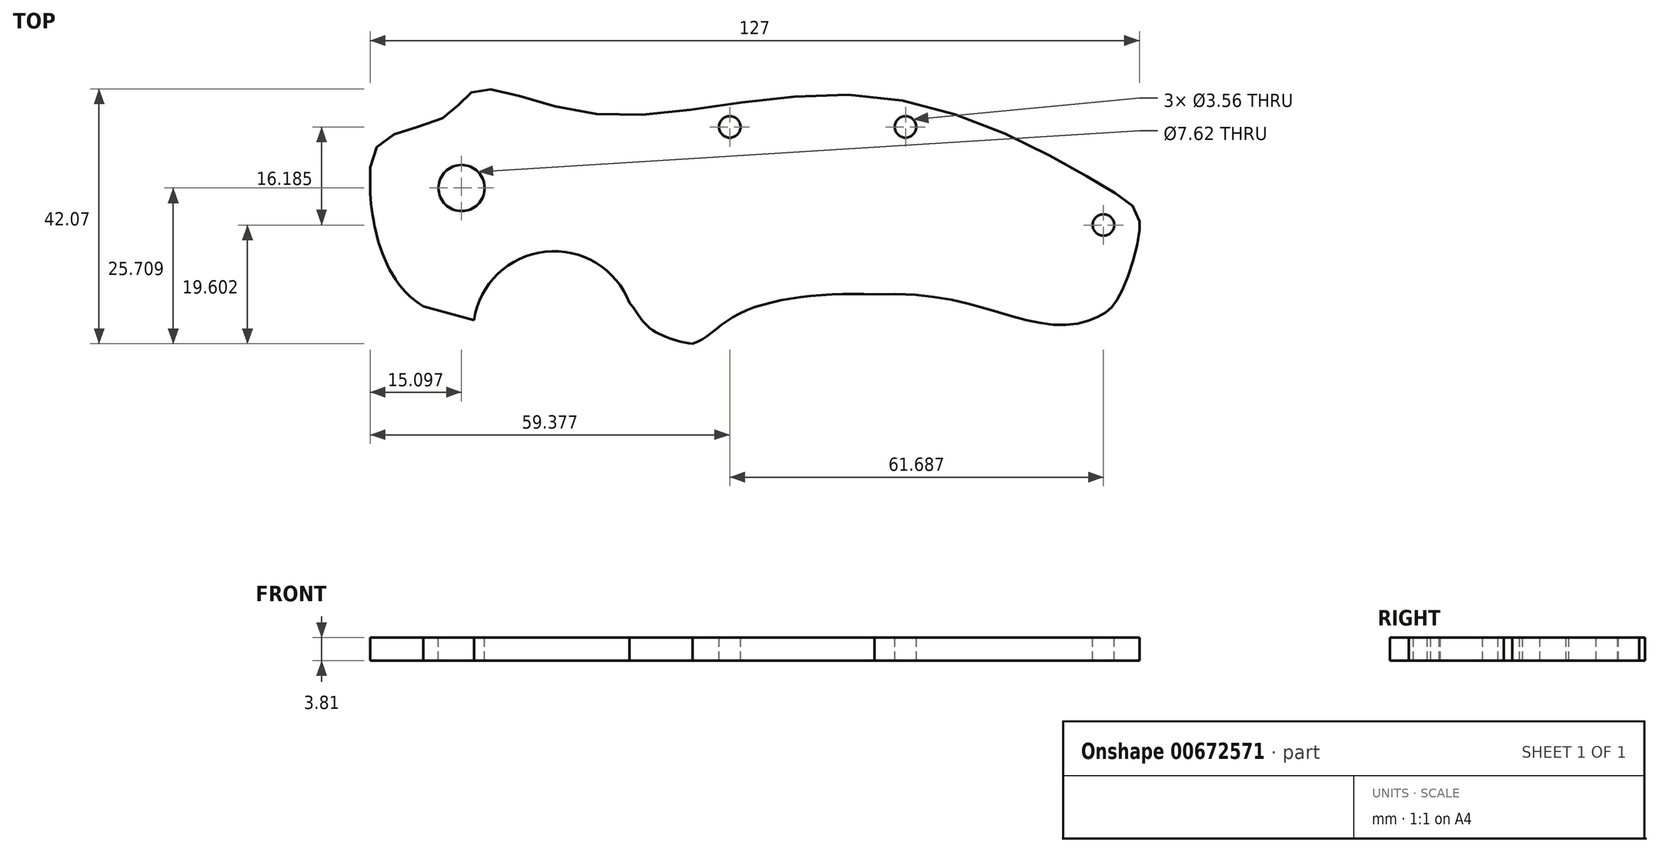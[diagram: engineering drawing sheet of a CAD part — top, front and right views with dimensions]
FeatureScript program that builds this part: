
annotation { "Feature Type Name" : "Feature", "Feature Type Description" : "" }
export const myFeature = defineFeature(function(context is Context, id is Id, definition is map)
    precondition{}
    {
        {
            var Q0;
            Q0=qCreatedBy(makeId("Top.planeOp"),FACE);
            var sketch = newSketch(context, id + "F0", { "sketchPlane" : qUnion([Q0])});
            skLineSegment(sketch, "E0.bottom", {"start": v(63.5, -38.1) * mm, "end": v(-63.5, -38.1) * mm});
            skLineSegment(sketch, "E0.top", {"start": v(63.5, 38.1) * mm, "end": v(-63.5, 38.1) * mm});
            skLineSegment(sketch, "E0.left", {"start": v(63.5, -38.1) * mm, "end": v(63.5, 38.1) * mm});
            skLineSegment(sketch, "E0.right", {"start": v(-63.5, -38.1) * mm, "end": v(-63.5, 38.1) * mm});
            skPoint(sketch, "E0.middle", {"position": v(0, 0) * mm});
            skSolve(sketch);
        }
        {
            var Q0;
            Q0=makeQuery(id+"F0.imprint","IMPRINT",FACE,{"disambiguationData":[TD([[makeQuery(id+"F0.imprint","IMPRINT",EDGE,{"derivedFrom":sQuery(id+"F0.wireOp",EDGE,"E0.bottom")}),-1.0]])]});
            extrude(context, id + "F1", {"entities" : qUnion([Q0]), "depth" : 3.8 * mm, "offsetDistance" : 25.4 * mm});
        }
        {
            var Q0;
            Q0=makeQuery(id+"F1.opExtrude","CAP_FACE",FACE,{"disambiguationData":[OSD([sQuery(id+"F0.wireOp",EDGE,"E0.bottom"),sQuery(id+"F0.wireOp",EDGE,"E0.top"),sQuery(id+"F0.wireOp",EDGE,"E0.left"),sQuery(id+"F0.wireOp",EDGE,"E0.right")])],"isStart":false});
            var sketch = newSketch(context, id + "F2", { "sketchPlane" : qUnion([Q0])});
            skFitSpline(sketch, "E1", {"points": [v(-63.5, 16.64) * mm, v(-61.23, 25.5) * mm, v(-50.85, 29.47) * mm, v(-45.96, 33.74) * mm, v(-26.11, 29.77) * mm, v(21.22, 32.52) * mm, v(59.1, 16.95) * mm, v(63.5, 12.06) * mm, v(60.31, 0) * mm, v(57.56, -3.2) * mm, v(51.46, -5.04) * mm, v(41.07, -3.2) * mm, v(25.5, 0) * mm, v(2.6, -3.51) * mm, v(-6.57, -8.1) * mm, v(-17.56, -5.34) * mm, v(-22.45, 0) * mm, v(-39.24, 0) * mm, v(-44.74, -4.12) * mm, v(-57.26, 0) * mm, v(-63.5, 16.64) * mm]});
            skSolve(sketch);
        }
        {
            var Q0;
            {var subQ5=makeQuery(id+"F1.opExtrude","CAP_EDGE",EDGE,{"disambiguationData":[OSD([sQuery(id+"F0.wireOp",EDGE,"E0.bottom")])],"isStart":false});Q0=makeQuery(id+"F2.imprint","IMPRINT",FACE,{"disambiguationData":[TD([[makeQuery(id+"F2.imprint","IMPRINT",EDGE,{"derivedFrom":subQ5}),-1.0]])]});}
            var Q1;
            {var subQ5=makeQuery(id+"F1.opExtrude","CAP_EDGE",EDGE,{"disambiguationData":[OSD([sQuery(id+"F0.wireOp",EDGE,"E0.top")])],"isStart":false});Q1=makeQuery(id+"F2.imprint","IMPRINT",FACE,{"disambiguationData":[TD([[makeQuery(id+"F2.imprint","IMPRINT",EDGE,{"derivedFrom":subQ5}),1.0]])]});}
            extrude(context, id + "F3", {"entities" : qUnion([Q0, Q1]), "operationType" : NewBodyOperationType.REMOVE, "endBound" : BoundingType.THROUGH_ALL, "oppositeDirection" : true, "depth" : 25.4 * mm, "offsetDistance" : 25.4 * mm});
        }
        {
            var Q0;
            Q0=makeQuery(id+"F1.opExtrude","CAP_FACE",FACE,{"disambiguationData":[OSD([sQuery(id+"F0.wireOp",EDGE,"E0.bottom"),sQuery(id+"F0.wireOp",EDGE,"E0.top"),sQuery(id+"F0.wireOp",EDGE,"E0.left"),sQuery(id+"F0.wireOp",EDGE,"E0.right")])],"isStart":false});
            var sketch = newSketch(context, id + "F4", { "sketchPlane" : qUnion([Q0])});
            skLineSegment(sketch, "E2", {"start": v(-54.7, -1.99) * mm, "end": v(-45.89, -4.38) * mm});
            skCircle(sketch, "E3", {"center": v(-33.13, -6.26) * mm, "radius": 13.38 * mm});
            skEllipse(sketch, "E4", {"center": v(16.34, -12.37) * mm, "majorRadius": 26.48 * mm, "minorRadius": 12.58 * mm, "majorAxis": v(1, 0.13)});
            skSolve(sketch);
        }
        {
            var Q0;
            {var subQ0=sQuery(id+"F4.wireOp",EDGE,"E3");var subQ1=sQuery(id+"F2.wireOp",EDGE,"E1");var subQ2=makeQuery(id+"F3.boolean.opBoolean","COPY",EDGE,{"derivedFrom":makeQuery(id+"F3.opExtrude","CAP_EDGE",EDGE,{"disambiguationData":[OSD([subQ1]),TDD([makeQuery(id+"F2.imprint","IMPRINT",EDGE,{"disambiguationData":[TD([[makeQuery(id+"F2.imprint","INTERSECT",VERTEX,{"disambiguationData":[OD(1.0)],"derivedFrom":[makeQuery(id+"F1.opExtrude","CAP_EDGE",EDGE,{"disambiguationData":[OSD([sQuery(id+"F0.wireOp",EDGE,"E0.right")])],"isStart":false}),subQ1]}),1.0]])],"derivedFrom":subQ1})])],"isStart":true})});var subQ3=makeQuery(id+"F4.imprint","INTERSECT",VERTEX,{"disambiguationData":[OD(0.0)],"derivedFrom":[subQ2,subQ0]});Q0=makeQuery(id+"F4.imprint","IMPRINT",FACE,{"disambiguationData":[TD([[makeQuery(id+"F4.imprint","IMPRINT",EDGE,{"disambiguationData":[TD([[subQ3,1.0]])],"derivedFrom":subQ0}),1.0]])]});}
            var Q1;
            {var subQ0=sQuery(id+"F4.wireOp",EDGE,"E2");var subQ4=sQuery(id+"F4.wireOp",EDGE,"E3");var subQ5=makeQuery(id+"F4.imprint","INTERSECT",VERTEX,{"derivedFrom":[subQ0,subQ4]});Q1=makeQuery(id+"F4.imprint","IMPRINT",FACE,{"disambiguationData":[TD([[makeQuery(id+"F4.imprint","IMPRINT",EDGE,{"disambiguationData":[TD([[subQ5,-1.0]])],"derivedFrom":subQ0}),1.0]])]});}
            var Q2;
            {var subQ0=sQuery(id+"F4.wireOp",EDGE,"E4");var subQ1=sQuery(id+"F2.wireOp",EDGE,"E1");var subQ2=makeQuery(id+"F3.boolean.opBoolean","COPY",EDGE,{"derivedFrom":makeQuery(id+"F3.opExtrude","CAP_EDGE",EDGE,{"disambiguationData":[OSD([subQ1]),TDD([makeQuery(id+"F2.imprint","IMPRINT",EDGE,{"disambiguationData":[TD([[makeQuery(id+"F2.imprint","INTERSECT",VERTEX,{"disambiguationData":[OD(1.0)],"derivedFrom":[makeQuery(id+"F1.opExtrude","CAP_EDGE",EDGE,{"disambiguationData":[OSD([sQuery(id+"F0.wireOp",EDGE,"E0.right")])],"isStart":false}),subQ1]}),1.0]])],"derivedFrom":subQ1})])],"isStart":true})});var subQ3=makeQuery(id+"F4.imprint","INTERSECT",VERTEX,{"disambiguationData":[OD(0.0)],"derivedFrom":[subQ2,subQ0]});Q2=makeQuery(id+"F4.imprint","IMPRINT",FACE,{"disambiguationData":[TD([[makeQuery(id+"F4.imprint","IMPRINT",EDGE,{"disambiguationData":[TD([[subQ3,1.0]])],"derivedFrom":subQ0}),1.0]])]});}
            var Q3;
            {var subQ0=sQuery(id+"F4.wireOp",EDGE,"E2");var subQ4=sQuery(id+"F4.wireOp",EDGE,"E3");var subQ5=makeQuery(id+"F4.imprint","INTERSECT",VERTEX,{"derivedFrom":[subQ0,subQ4]});Q3=makeQuery(id+"F4.imprint","IMPRINT",FACE,{"disambiguationData":[TD([[makeQuery(id+"F4.imprint","IMPRINT",EDGE,{"disambiguationData":[TD([[subQ5,1.0]])],"derivedFrom":subQ0}),-1.0]])]});}
            extrude(context, id + "F5", {"entities" : qUnion([Q0, Q1, Q2, Q3]), "operationType" : NewBodyOperationType.REMOVE, "endBound" : BoundingType.THROUGH_ALL, "oppositeDirection" : true, "depth" : 25.4 * mm, "offsetDistance" : 25.4 * mm});
        }
        {
            var Q0;
            {var subQ1=sQuery(id+"F0.wireOp",EDGE,"E0.right");var subQ3=sQuery(id+"F0.wireOp",EDGE,"E0.left");Q0=makeQuery(id+"F5.boolean.opBoolean","SPLIT",FACE,{"disambiguationData":[TD([makeQuery(id+"F1.opExtrude","SWEPT_FACE",FACE,{"disambiguationData":[OSD([subQ3])]})])],"derivedFrom":makeQuery(id+"F1.opExtrude","CAP_FACE",FACE,{"disambiguationData":[OSD([sQuery(id+"F0.wireOp",EDGE,"E0.bottom"),sQuery(id+"F0.wireOp",EDGE,"E0.top"),subQ3,subQ1])],"isStart":false})});}
            var sketch = newSketch(context, id + "F6", { "sketchPlane" : qUnion([Q0])});
            skFitSpline(sketch, "E5", {"points": [v(-23.23, 2.75) * mm, v(-17.4, -5.48) * mm, v(-10.24, -8.15) * mm, v(-2.58, -3.2) * mm, v(19.77, 0) * mm, v(43.26, -3.83) * mm, v(55.8, -10.53) * mm, v(42.96, -25.2) * mm, v(-17.87, -22.76) * mm, v(-23.23, 2.75) * mm]});
            skSolve(sketch);
        }
        {
            var Q0;
            {var subQ0=sQuery(id+"F6.wireOp",EDGE,"E5");var subQ1=sQuery(id+"F0.wireOp",EDGE,"E0.right");var subQ2=sQuery(id+"F0.wireOp",EDGE,"E0.left");var subQ3=sQuery(id+"F2.wireOp",EDGE,"E1");var subQ4=makeQuery(id+"F2.imprint","IMPRINT",EDGE,{"disambiguationData":[TD([[makeQuery(id+"F2.imprint","INTERSECT",VERTEX,{"disambiguationData":[OD(1.0)],"derivedFrom":[makeQuery(id+"F1.opExtrude","CAP_EDGE",EDGE,{"disambiguationData":[OSD([subQ1])],"isStart":false}),subQ3]}),1.0]])],"derivedFrom":subQ3});var subQ6=makeQuery(id+"F3.boolean.opBoolean","COPY",EDGE,{"derivedFrom":makeQuery(id+"F3.opExtrude","CAP_EDGE",EDGE,{"disambiguationData":[OSD([subQ3]),TDD([subQ4])],"isStart":true})});var subQ8=makeQuery(id+"F5.boolean.opBoolean","SPLIT",EDGE,{"disambiguationData":[TD([makeQuery(id+"F1.opExtrude","SWEPT_FACE",FACE,{"disambiguationData":[OSD([subQ2])]})])],"derivedFrom":subQ6});var subQ9=makeQuery(id+"F6.imprint","INTERSECT",VERTEX,{"disambiguationData":[OD(2.0)],"derivedFrom":[subQ8,subQ0]});Q0=makeQuery(id+"F6.imprint","IMPRINT",FACE,{"disambiguationData":[TD([[makeQuery(id+"F6.imprint","IMPRINT",EDGE,{"disambiguationData":[TD([[subQ9,-1.0]])],"derivedFrom":subQ0}),-1.0]])]});}
            extrude(context, id + "F7", {"entities" : qUnion([Q0]), "operationType" : NewBodyOperationType.REMOVE, "endBound" : BoundingType.THROUGH_ALL, "oppositeDirection" : true, "depth" : 25.4 * mm, "offsetDistance" : 25.4 * mm});
        }
        {
            var Q0;
            {var subQ1=sQuery(id+"F0.wireOp",EDGE,"E0.right");var subQ3=sQuery(id+"F0.wireOp",EDGE,"E0.left");Q0=makeQuery(id+"F5.boolean.opBoolean","SPLIT",FACE,{"disambiguationData":[TD([makeQuery(id+"F1.opExtrude","SWEPT_FACE",FACE,{"disambiguationData":[OSD([subQ3])]})])],"derivedFrom":makeQuery(id+"F1.opExtrude","CAP_FACE",FACE,{"disambiguationData":[OSD([sQuery(id+"F0.wireOp",EDGE,"E0.bottom"),sQuery(id+"F0.wireOp",EDGE,"E0.top"),subQ3,subQ1])],"isStart":false})});}
            var sketch = newSketch(context, id + "F8", { "sketchPlane" : qUnion([Q0])});
            skLineSegment(sketch, "E6", {"start": v(-17.57, -8.87) * mm, "end": v(3.3, -6.1) * mm});
            skLineSegment(sketch, "E7", {"start": v(3.3, -6.1) * mm, "end": v(-7.14, -16.53) * mm});
            skLineSegment(sketch, "E8", {"start": v(-7.14, -16.53) * mm, "end": v(-17.57, -8.87) * mm});
            skSolve(sketch);
        }
        {
            var Q0;
            {var subQ0=sQuery(id+"F8.wireOp",EDGE,"E6");var subQ11=sQuery(id+"F6.wireOp",EDGE,"E5");var subQ14=makeQuery(id+"F7.boolean.opBoolean","COPY",EDGE,{"derivedFrom":makeQuery(id+"F7.opExtrude","CAP_EDGE",EDGE,{"disambiguationData":[OSD([subQ11])],"isStart":true})});var subQ15=makeQuery(id+"F8.imprint","INTERSECT",VERTEX,{"derivedFrom":[subQ14,subQ0]});Q0=makeQuery(id+"F8.imprint","IMPRINT",FACE,{"disambiguationData":[TD([[makeQuery(id+"F8.imprint","IMPRINT",EDGE,{"disambiguationData":[TD([[subQ15,1.0]])],"derivedFrom":subQ0}),-1.0]])]});}
            extrude(context, id + "F9", {"entities" : qUnion([Q0]), "operationType" : NewBodyOperationType.REMOVE, "endBound" : BoundingType.THROUGH_ALL, "oppositeDirection" : true, "depth" : 25.4 * mm, "offsetDistance" : 25.4 * mm});
        }
        {
            var Q0;
            {var subQ1=sQuery(id+"F0.wireOp",EDGE,"E0.right");var subQ3=sQuery(id+"F0.wireOp",EDGE,"E0.left");Q0=makeQuery(id+"F5.boolean.opBoolean","SPLIT",FACE,{"disambiguationData":[TD([makeQuery(id+"F1.opExtrude","SWEPT_FACE",FACE,{"disambiguationData":[OSD([subQ3])]})])],"derivedFrom":makeQuery(id+"F1.opExtrude","CAP_FACE",FACE,{"disambiguationData":[OSD([sQuery(id+"F0.wireOp",EDGE,"E0.bottom"),sQuery(id+"F0.wireOp",EDGE,"E0.top"),subQ3,subQ1])],"isStart":false})});}
            var sketch = newSketch(context, id + "F10", { "sketchPlane" : qUnion([Q0])});
            skLineSegment(sketch, "E9", {"start": v(-47.84, -5.25) * mm, "end": v(-44.37, -2.7) * mm});
            skLineSegment(sketch, "E10", {"start": v(-44.37, -2.7) * mm, "end": v(-44.37, -5.15) * mm});
            skLineSegment(sketch, "E11", {"start": v(-44.37, -5.15) * mm, "end": v(-47.84, -5.25) * mm});
            skSolve(sketch);
        }
        {
            var Q0;
            {var subQ1=sQuery(id+"F10.wireOp",EDGE,"E10");Q0=makeQuery(id+"F10.imprint","IMPRINT",FACE,{"disambiguationData":[TD([[makeQuery(id+"F10.imprint","IMPRINT",EDGE,{"derivedFrom":subQ1}),-1.0]])]});}
            extrude(context, id + "F11", {"entities" : qUnion([Q0]), "operationType" : NewBodyOperationType.REMOVE, "endBound" : BoundingType.THROUGH_ALL, "oppositeDirection" : true, "depth" : 25.4 * mm, "offsetDistance" : 25.4 * mm});
        }
        {
            var Q0;
            {var subQ1=sQuery(id+"F0.wireOp",EDGE,"E0.right");var subQ3=sQuery(id+"F0.wireOp",EDGE,"E0.left");Q0=makeQuery(id+"F5.boolean.opBoolean","SPLIT",FACE,{"disambiguationData":[TD([makeQuery(id+"F1.opExtrude","SWEPT_FACE",FACE,{"disambiguationData":[OSD([subQ3])]})])],"derivedFrom":makeQuery(id+"F1.opExtrude","CAP_FACE",FACE,{"disambiguationData":[OSD([sQuery(id+"F0.wireOp",EDGE,"E0.bottom"),sQuery(id+"F0.wireOp",EDGE,"E0.top"),subQ3,subQ1])],"isStart":false})});}
            var sketch = newSketch(context, id + "F12", { "sketchPlane" : qUnion([Q0])});
            skCircle(sketch, "E12", {"center": v(-48.4, 17.56) * mm, "radius": 3.81 * mm});
            skCircle(sketch, "E13", {"center": v(-4.12, 27.64) * mm, "radius": 1.78 * mm});
            skCircle(sketch, "E14", {"center": v(24.89, 27.64) * mm, "radius": 1.78 * mm});
            skCircle(sketch, "E15", {"center": v(57.56, 11.45) * mm, "radius": 1.78 * mm});
            skSolve(sketch);
        }
        {
            var Q0;
            Q0=makeQuery(id+"F12.imprint","IMPRINT",FACE,{"disambiguationData":[TD([[makeQuery(id+"F12.imprint","IMPRINT",EDGE,{"derivedFrom":sQuery(id+"F12.wireOp",EDGE,"E12")}),1.0]])]});
            var Q1;
            Q1=makeQuery(id+"F12.imprint","IMPRINT",FACE,{"disambiguationData":[TD([[makeQuery(id+"F12.imprint","IMPRINT",EDGE,{"derivedFrom":sQuery(id+"F12.wireOp",EDGE,"E13")}),1.0]])]});
            var Q2;
            Q2=makeQuery(id+"F12.imprint","IMPRINT",FACE,{"disambiguationData":[TD([[makeQuery(id+"F12.imprint","IMPRINT",EDGE,{"derivedFrom":sQuery(id+"F12.wireOp",EDGE,"E14")}),1.0]])]});
            var Q3;
            Q3=makeQuery(id+"F12.imprint","IMPRINT",FACE,{"disambiguationData":[TD([[makeQuery(id+"F12.imprint","IMPRINT",EDGE,{"derivedFrom":sQuery(id+"F12.wireOp",EDGE,"E15")}),1.0]])]});
            extrude(context, id + "F13", {"entities" : qUnion([Q0, Q1, Q2, Q3]), "operationType" : NewBodyOperationType.REMOVE, "endBound" : BoundingType.THROUGH_ALL, "oppositeDirection" : true, "depth" : 25.4 * mm, "offsetDistance" : 25.4 * mm});
        }
    });
